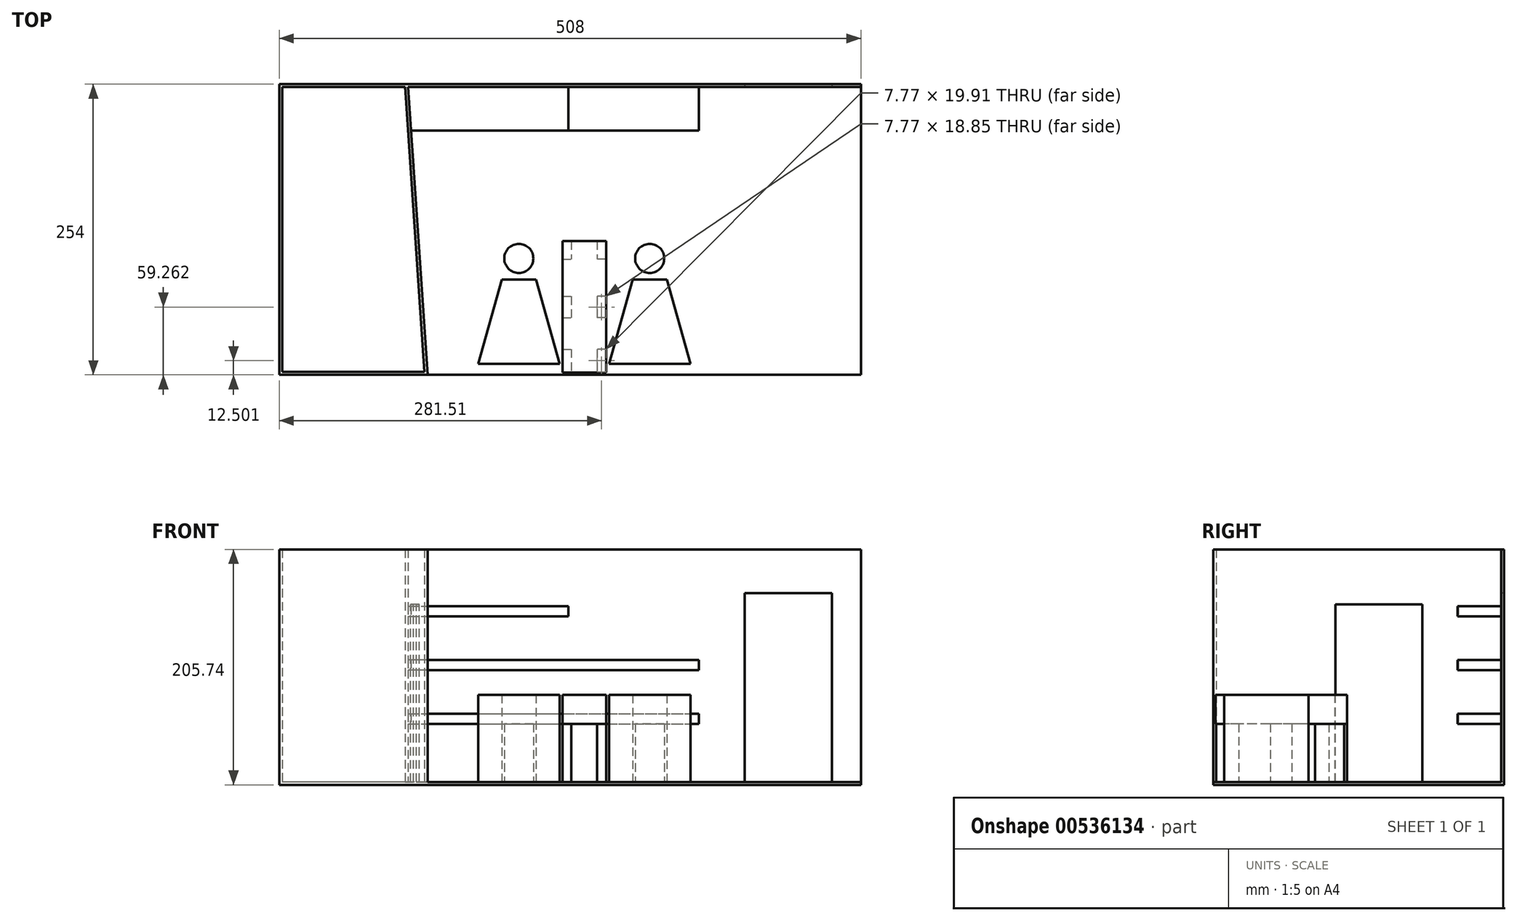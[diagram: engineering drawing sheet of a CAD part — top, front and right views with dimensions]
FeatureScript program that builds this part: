
annotation { "Feature Type Name" : "Feature", "Feature Type Description" : "" }
export const myFeature = defineFeature(function(context is Context, id is Id, definition is map)
    precondition{}
    {
        {
            var Q0;
            Q0=qCreatedBy(makeId("Top.planeOp"),FACE);
            var sketch = newSketch(context, id + "F0", { "sketchPlane" : qUnion([Q0])});
            skLineSegment(sketch, "E0.bottom", {"start": v(-252.39, 62) * mm, "end": v(255.61, 62) * mm});
            skLineSegment(sketch, "E0.top", {"start": v(-252.39, -192) * mm, "end": v(255.61, -192) * mm});
            skLineSegment(sketch, "E0.left", {"start": v(-252.39, 62) * mm, "end": v(-252.39, -192) * mm});
            skLineSegment(sketch, "E0.right", {"start": v(255.61, 62) * mm, "end": v(255.61, -192) * mm});
            skSolve(sketch);
        }
        {
            var Q0;
            Q0=makeQuery(id+"F0.imprint","IMPRINT",FACE,{"disambiguationData":[TD([[makeQuery(id+"F0.imprint","IMPRINT",EDGE,{"derivedFrom":sQuery(id+"F0.wireOp",EDGE,"E0.bottom")}),-1.0]])]});
            extrude(context, id + "F1", {"entities" : qUnion([Q0]), "depth" : 2.54 * mm, "offsetDistance" : 25.4 * mm});
        }
        {
            var Q0;
            Q0=makeQuery(id+"F1.opExtrude","CAP_FACE",FACE,{"disambiguationData":[OSD([sQuery(id+"F0.wireOp",EDGE,"E0.bottom"),sQuery(id+"F0.wireOp",EDGE,"E0.top"),sQuery(id+"F0.wireOp",EDGE,"E0.left"),sQuery(id+"F0.wireOp",EDGE,"E0.right")])],"isStart":false});
            var sketch = newSketch(context, id + "F2", { "sketchPlane" : qUnion([Q0])});
            skLineSegment(sketch, "E1", {"start": v(-252.39, -192) * mm, "end": v(-252.39, 62) * mm});
            skLineSegment(sketch, "E2", {"start": v(-252.39, 62) * mm, "end": v(255.61, 62) * mm});
            skLineSegment(sketch, "E3", {"start": v(255.61, 62) * mm, "end": v(255.61, 59.45) * mm});
            skLineSegment(sketch, "E4", {"start": v(255.61, 59.45) * mm, "end": v(-249.85, 59.45) * mm});
            skLineSegment(sketch, "E5", {"start": v(-249.85, 59.45) * mm, "end": v(-249.85, -192) * mm});
            skLineSegment(sketch, "E6", {"start": v(-249.85, -192) * mm, "end": v(-252.39, -192) * mm});
            skSolve(sketch);
        }
        {
            var Q0;
            Q0 = qSketchRegion(id + "F2", true);
            extrude(context, id + "F3", {"entities" : qUnion([Q0]), "operationType" : NewBodyOperationType.ADD, "depth" : 203.2 * mm, "offsetDistance" : 25.4 * mm});
        }
        {
            var Q0;
            Q0=makeQuery(id+"F1.opExtrude","CAP_FACE",FACE,{"disambiguationData":[OSD([sQuery(id+"F0.wireOp",EDGE,"E0.bottom"),sQuery(id+"F0.wireOp",EDGE,"E0.top"),sQuery(id+"F0.wireOp",EDGE,"E0.left"),sQuery(id+"F0.wireOp",EDGE,"E0.right")])],"isStart":false});
            var sketch = newSketch(context, id + "F4", { "sketchPlane" : qUnion([Q0])});
            skLineSegment(sketch, "E7.top", {"start": v(-249.85, -192) * mm, "end": v(-122.85, -192) * mm});
            skLineSegment(sketch, "E7.right", {"start": v(-139.97, 59.45) * mm, "end": v(-122.85, -192) * mm});
            skLineSegment(sketch, "E8", {"start": v(-139.97, 59.45) * mm, "end": v(-142.51, 59.45) * mm});
            skLineSegment(sketch, "E9", {"start": v(-142.51, 59.45) * mm, "end": v(-125.56, -189.47) * mm});
            skLineSegment(sketch, "E10", {"start": v(-125.56, -189.47) * mm, "end": v(-249.85, -189.47) * mm});
            skLineSegment(sketch, "E11", {"start": v(-249.85, -189.47) * mm, "end": v(-249.85, -192) * mm});
            skSolve(sketch);
        }
        {
            var Q0;
            Q0 = qSketchRegion(id + "F4", true);
            extrude(context, id + "F5", {"entities" : qUnion([Q0]), "operationType" : NewBodyOperationType.ADD, "depth" : 203.2 * mm, "offsetDistance" : 25.4 * mm});
        }
        {
            var Q0;
            Q0=makeQuery(id+"F5.opExtrude","SWEPT_FACE",FACE,{"disambiguationData":[OSD([sQuery(id+"F4.wireOp",EDGE,"E7.right")])]});
            var sketch = newSketch(context, id + "F6", { "sketchPlane" : qUnion([Q0])});
            skLineSegment(sketch, "E12.bottom", {"start": v(-76.2, 2.54) * mm, "end": v(0, 2.54) * mm});
            skLineSegment(sketch, "E12.top", {"start": v(-76.2, 157.64) * mm, "end": v(0, 157.64) * mm});
            skLineSegment(sketch, "E12.left", {"start": v(-76.2, 2.54) * mm, "end": v(-76.2, 157.64) * mm});
            skLineSegment(sketch, "E12.right", {"start": v(0, 2.54) * mm, "end": v(0, 157.64) * mm});
            skSolve(sketch);
        }
        {
            var Q0;
            Q0 = qSketchRegion(id + "F6", true);
            extrude(context, id + "F7", {"entities" : qUnion([Q0]), "operationType" : NewBodyOperationType.REMOVE, "oppositeDirection" : true, "depth" : 25.4 * mm, "offsetDistance" : 25.4 * mm});
        }
        {
            var Q0;
            {var subQ1=sQuery(id+"F0.wireOp",EDGE,"E0.right");var subQ2=sQuery(id+"F0.wireOp",EDGE,"E0.top");var subQ3=makeQuery(id+"F1.opExtrude","CAP_FACE",FACE,{"disambiguationData":[OSD([sQuery(id+"F0.wireOp",EDGE,"E0.bottom"),subQ2,sQuery(id+"F0.wireOp",EDGE,"E0.left"),subQ1])],"isStart":false});Q0=makeQuery(id+"F7.boolean.opBoolean","MERGE",FACE,{"derivedFrom":[makeQuery(id+"F5.boolean.opBoolean","SPLIT",FACE,{"disambiguationData":[TD([makeQuery(id+"F1.opExtrude","SWEPT_FACE",FACE,{"disambiguationData":[OSD([subQ2])]})])],"derivedFrom":subQ3}),makeQuery(id+"F5.boolean.opBoolean","SPLIT",FACE,{"disambiguationData":[TD([makeQuery(id+"F3.opExtrude","SWEPT_FACE",FACE,{"disambiguationData":[OSD([sQuery(id+"F2.wireOp",EDGE,"E5")])]})])],"derivedFrom":subQ3}),makeQuery(id+"F7.opExtrude","SWEPT_FACE",FACE,{"disambiguationData":[OSD([sQuery(id+"F6.wireOp",EDGE,"E12.bottom")])]})]});}
            var sketch = newSketch(context, id + "F8", { "sketchPlane" : qUnion([Q0])});
            skLineSegment(sketch, "E13", {"start": v(-43.2, -182.35) * mm, "end": v(-7.63, -182.35) * mm});
            skLineSegment(sketch, "E14", {"start": v(-7.63, -182.35) * mm, "end": v(-28.26, -108.75) * mm});
            skLineSegment(sketch, "E15", {"start": v(-28.26, -108.75) * mm, "end": v(-43.2, -108.75) * mm});
            skPoint(sketch, "E15.endSnap0", {"position": v(-43.2, -182.35) * mm});
            skLineSegment(sketch, "E16", {"start": v(-43.2, -108.75) * mm, "end": v(-43.2, -182.35) * mm, "construction": true});
            skPoint(sketch, "E17.orphan", {"position": v(-78.75, -182.35) * mm});
            skLineSegment(sketch, "E18.MirrorCS", {"start": v(-78.75, -182.35) * mm, "end": v(-58.13, -108.75) * mm});
            skLineSegment(sketch, "E19.MirrorCS", {"start": v(-58.13, -108.75) * mm, "end": v(-43.2, -108.75) * mm});
            skLineSegment(sketch, "E20.MirrorCS", {"start": v(-43.2, -182.35) * mm, "end": v(-78.75, -182.35) * mm});
            skSolve(sketch);
        }
        {
            var Q0;
            Q0=makeQuery(id+"F8.imprint","IMPRINT",FACE,{"disambiguationData":[TD([[makeQuery(id+"F8.imprint","IMPRINT",EDGE,{"derivedFrom":sQuery(id+"F8.wireOp",EDGE,"E13")}),1.0]])]});
            extrude(context, id + "F9", {"entities" : qUnion([Q0]), "operationType" : NewBodyOperationType.ADD, "depth" : 76.2 * mm, "offsetDistance" : 25.4 * mm});
        }
        {
            var Q0;
            {var subQ1=sQuery(id+"F0.wireOp",EDGE,"E0.right");var subQ2=sQuery(id+"F0.wireOp",EDGE,"E0.top");var subQ3=makeQuery(id+"F1.opExtrude","CAP_FACE",FACE,{"disambiguationData":[OSD([sQuery(id+"F0.wireOp",EDGE,"E0.bottom"),subQ2,sQuery(id+"F0.wireOp",EDGE,"E0.left"),subQ1])],"isStart":false});Q0=makeQuery(id+"F7.boolean.opBoolean","MERGE",FACE,{"derivedFrom":[makeQuery(id+"F5.boolean.opBoolean","SPLIT",FACE,{"disambiguationData":[TD([makeQuery(id+"F1.opExtrude","SWEPT_FACE",FACE,{"disambiguationData":[OSD([subQ2])]})])],"derivedFrom":subQ3}),makeQuery(id+"F5.boolean.opBoolean","SPLIT",FACE,{"disambiguationData":[TD([makeQuery(id+"F3.opExtrude","SWEPT_FACE",FACE,{"disambiguationData":[OSD([sQuery(id+"F2.wireOp",EDGE,"E5")])]})])],"derivedFrom":subQ3}),makeQuery(id+"F7.opExtrude","SWEPT_FACE",FACE,{"disambiguationData":[OSD([sQuery(id+"F6.wireOp",EDGE,"E12.bottom")])]})]});}
            var sketch = newSketch(context, id + "F10", { "sketchPlane" : qUnion([Q0])});
            skLineSegment(sketch, "E21.bottom", {"start": v(-5.1, -189.47) * mm, "end": v(33, -189.47) * mm, "construction": true});
            skLineSegment(sketch, "E21.top", {"start": v(-5.1, -75.17) * mm, "end": v(33, -75.17) * mm, "construction": true});
            skLineSegment(sketch, "E21.left", {"start": v(-5.1, -189.47) * mm, "end": v(-5.1, -75.17) * mm, "construction": true});
            skLineSegment(sketch, "E21.right", {"start": v(33, -189.47) * mm, "end": v(33, -75.17) * mm, "construction": true});
            skLineSegment(sketch, "E22.bottom", {"start": v(-5.1, -75.17) * mm, "end": v(2.68, -75.17) * mm});
            skLineSegment(sketch, "E22.top", {"start": v(-5.1, -90.97) * mm, "end": v(2.68, -90.97) * mm});
            skLineSegment(sketch, "E22.left", {"start": v(-5.1, -75.17) * mm, "end": v(-5.1, -90.97) * mm});
            skLineSegment(sketch, "E22.right", {"start": v(2.68, -75.17) * mm, "end": v(2.68, -90.97) * mm});
            skLineSegment(sketch, "E23.bottom", {"start": v(-5.1, -123.32) * mm, "end": v(2.68, -123.32) * mm});
            skLineSegment(sketch, "E23.top", {"start": v(-5.1, -142.17) * mm, "end": v(2.68, -142.17) * mm});
            skLineSegment(sketch, "E23.left", {"start": v(-5.1, -123.32) * mm, "end": v(-5.1, -142.17) * mm});
            skLineSegment(sketch, "E23.right", {"start": v(2.68, -123.32) * mm, "end": v(2.68, -142.17) * mm});
            skLineSegment(sketch, "E24.bottom", {"start": v(-5.1, -169.55) * mm, "end": v(2.68, -169.55) * mm});
            skLineSegment(sketch, "E24.top", {"start": v(-5.1, -189.47) * mm, "end": v(2.68, -189.47) * mm});
            skLineSegment(sketch, "E24.left", {"start": v(-5.1, -169.55) * mm, "end": v(-5.1, -189.47) * mm});
            skLineSegment(sketch, "E24.right", {"start": v(2.68, -169.55) * mm, "end": v(2.68, -189.47) * mm});
            skLineSegment(sketch, "E25", {"start": v(13.96, -75.17) * mm, "end": v(13.96, -189.47) * mm, "construction": true});
            skLineSegment(sketch, "E26.MirrorCS", {"start": v(25.23, -75.17) * mm, "end": v(25.23, -90.97) * mm});
            skLineSegment(sketch, "E27.MirrorCS", {"start": v(33, -90.97) * mm, "end": v(25.23, -90.97) * mm});
            skLineSegment(sketch, "E28.MirrorCS", {"start": v(33, -123.32) * mm, "end": v(25.23, -123.32) * mm});
            skLineSegment(sketch, "E29.MirrorCS", {"start": v(25.23, -123.32) * mm, "end": v(25.23, -142.17) * mm});
            skLineSegment(sketch, "E30.MirrorCS", {"start": v(33, -142.17) * mm, "end": v(25.23, -142.17) * mm});
            skLineSegment(sketch, "E31.MirrorCS", {"start": v(33, -169.55) * mm, "end": v(25.23, -169.55) * mm});
            skLineSegment(sketch, "E32.MirrorCS", {"start": v(25.23, -169.55) * mm, "end": v(25.23, -189.47) * mm});
            skLineSegment(sketch, "E33", {"start": v(25.23, -75.17) * mm, "end": v(33, -75.17) * mm, "construction": true});
            skLineSegment(sketch, "E34", {"start": v(33, -75.17) * mm, "end": v(25.23, -75.17) * mm});
            skLineSegment(sketch, "E35", {"start": v(33, -75.17) * mm, "end": v(33, -90.97) * mm});
            skLineSegment(sketch, "E36", {"start": v(33, -123.32) * mm, "end": v(33, -142.17) * mm});
            skLineSegment(sketch, "E37", {"start": v(33, -169.55) * mm, "end": v(33, -189.47) * mm});
            skLineSegment(sketch, "E38.MirrorCS", {"start": v(56.17, -108.75) * mm, "end": v(86.04, -108.75) * mm});
            skLineSegment(sketch, "E39.MirrorCS", {"start": v(35.55, -182.35) * mm, "end": v(56.17, -108.75) * mm});
            skLineSegment(sketch, "E40.MirrorCS", {"start": v(86.04, -108.75) * mm, "end": v(106.67, -182.35) * mm});
            skLineSegment(sketch, "E41.MirrorCS", {"start": v(106.67, -182.35) * mm, "end": v(35.55, -182.35) * mm});
            skLineSegment(sketch, "E42", {"start": v(25.23, -189.47) * mm, "end": v(33, -189.47) * mm});
            skPoint(sketch, "E43.0.0.start.orphan", {"position": v(-58.13, -108.75) * mm});
            skPoint(sketch, "E43.0.2.end.orphan", {"position": v(-28.26, -108.75) * mm});
            skPoint(sketch, "E43.0.1.end.orphan", {"position": v(-7.63, -182.35) * mm});
            skPoint(sketch, "E43.0.1.start.orphan", {"position": v(-78.75, -182.35) * mm});
            skSolve(sketch);
        }
        {
            var Q0;
            Q0 = qSketchRegion(id + "F10", true);
            extrude(context, id + "F11", {"entities" : qUnion([Q0]), "operationType" : NewBodyOperationType.ADD, "depth" : 76.2 * mm, "offsetDistance" : 25.4 * mm});
        }
        {
            var Q0;
            Q0=makeQuery(id+"F11.opExtrude","CAP_FACE",FACE,{"disambiguationData":[OSD([sQuery(id+"F10.wireOp",EDGE,"E22.bottom"),sQuery(id+"F10.wireOp",EDGE,"E22.top"),sQuery(id+"F10.wireOp",EDGE,"E22.left"),sQuery(id+"F10.wireOp",EDGE,"E22.right")])],"isStart":false});
            var sketch = newSketch(context, id + "F12", { "sketchPlane" : qUnion([Q0])});
            skLineSegment(sketch, "E44.bottom", {"start": v(-5.1, -75.17) * mm, "end": v(33.24, -75.17) * mm});
            skLineSegment(sketch, "E44.top", {"start": v(-5.1, -189.9) * mm, "end": v(33.24, -189.9) * mm});
            skLineSegment(sketch, "E44.left", {"start": v(-5.1, -75.17) * mm, "end": v(-5.1, -189.9) * mm});
            skLineSegment(sketch, "E44.right", {"start": v(33.24, -75.17) * mm, "end": v(33.24, -189.9) * mm});
            skSolve(sketch);
        }
        {
            var Q0;
            Q0 = qSketchRegion(id + "F12", true);
            extrude(context, id + "F13", {"entities" : qUnion([Q0]), "operationType" : NewBodyOperationType.ADD, "oppositeDirection" : true, "depth" : 25.4 * mm, "offsetDistance" : 25.4 * mm});
        }
        {
            var Q0;
            {var subQ1=sQuery(id+"F0.wireOp",EDGE,"E0.right");var subQ2=sQuery(id+"F0.wireOp",EDGE,"E0.top");var subQ3=makeQuery(id+"F1.opExtrude","CAP_FACE",FACE,{"disambiguationData":[OSD([sQuery(id+"F0.wireOp",EDGE,"E0.bottom"),subQ2,sQuery(id+"F0.wireOp",EDGE,"E0.left"),subQ1])],"isStart":false});Q0=makeQuery(id+"F7.boolean.opBoolean","MERGE",FACE,{"derivedFrom":[makeQuery(id+"F5.boolean.opBoolean","SPLIT",FACE,{"disambiguationData":[TD([makeQuery(id+"F1.opExtrude","SWEPT_FACE",FACE,{"disambiguationData":[OSD([subQ2])]})])],"derivedFrom":subQ3}),makeQuery(id+"F5.boolean.opBoolean","SPLIT",FACE,{"disambiguationData":[TD([makeQuery(id+"F3.opExtrude","SWEPT_FACE",FACE,{"disambiguationData":[OSD([sQuery(id+"F2.wireOp",EDGE,"E5")])]})])],"derivedFrom":subQ3}),makeQuery(id+"F7.opExtrude","SWEPT_FACE",FACE,{"disambiguationData":[OSD([sQuery(id+"F6.wireOp",EDGE,"E12.bottom")])]})]});}
            var sketch = newSketch(context, id + "F14", { "sketchPlane" : qUnion([Q0])});
            skCircle(sketch, "E45", {"center": v(-43.2, -90.25) * mm, "radius": 12.7 * mm});
            skPoint(sketch, "E45.centerSnap0", {"position": v(-43.2, -108.75) * mm});
            skCircle(sketch, "E46", {"center": v(71.1, -90.25) * mm, "radius": 12.7 * mm});
            skPoint(sketch, "E47", {"position": v(71.1, -108.75) * mm});
            skSolve(sketch);
        }
        {
            var Q0;
            Q0 = qSketchRegion(id + "F14", true);
            extrude(context, id + "F15", {"entities" : qUnion([Q0]), "operationType" : NewBodyOperationType.ADD, "depth" : 50.8 * mm, "offsetDistance" : 25.4 * mm});
        }
        {
            var Q0;
            {var subQ0=sQuery(id+"F2.wireOp",EDGE,"E4");var subQ2=sQuery(id+"F0.wireOp",EDGE,"E0.right");Q0=makeQuery(id+"F5.boolean.opBoolean","SPLIT",FACE,{"disambiguationData":[TD([makeQuery(id+"F1.opExtrude","SWEPT_FACE",FACE,{"disambiguationData":[OSD([subQ2])]})])],"derivedFrom":makeQuery(id+"F3.opExtrude","SWEPT_FACE",FACE,{"disambiguationData":[OSD([subQ0])]})});}
            var sketch = newSketch(context, id + "F16", { "sketchPlane" : qUnion([Q0])});
            skLineSegment(sketch, "E48.bottom", {"start": v(154.01, 2.54) * mm, "end": v(230.21, 2.54) * mm});
            skLineSegment(sketch, "E48.top", {"start": v(154.01, 167.64) * mm, "end": v(230.21, 167.64) * mm});
            skLineSegment(sketch, "E48.left", {"start": v(154.01, 2.54) * mm, "end": v(154.01, 167.64) * mm});
            skLineSegment(sketch, "E48.right", {"start": v(230.21, 2.54) * mm, "end": v(230.21, 167.64) * mm});
            skSolve(sketch);
        }
        {
            var Q0;
            Q0 = qSketchRegion(id + "F16", true);
            extrude(context, id + "F17", {"entities" : qUnion([Q0]), "operationType" : NewBodyOperationType.REMOVE, "oppositeDirection" : true, "depth" : 25.4 * mm, "offsetDistance" : 25.4 * mm});
        }
        {
            var Q0;
            {var subQ0=sQuery(id+"F2.wireOp",EDGE,"E4");var subQ2=sQuery(id+"F0.wireOp",EDGE,"E0.right");Q0=makeQuery(id+"F5.boolean.opBoolean","SPLIT",FACE,{"disambiguationData":[TD([makeQuery(id+"F1.opExtrude","SWEPT_FACE",FACE,{"disambiguationData":[OSD([subQ2])]})])],"derivedFrom":makeQuery(id+"F3.opExtrude","SWEPT_FACE",FACE,{"disambiguationData":[OSD([subQ0])]})});}
            var sketch = newSketch(context, id + "F18", { "sketchPlane" : qUnion([Q0])});
            skLineSegment(sketch, "E49.bottom", {"start": v(-139.97, 53.34) * mm, "end": v(114.03, 53.34) * mm});
            skLineSegment(sketch, "E49.top", {"start": v(-139.97, 62.23) * mm, "end": v(114.03, 62.23) * mm});
            skLineSegment(sketch, "E49.left", {"start": v(-139.97, 53.34) * mm, "end": v(-139.97, 62.23) * mm});
            skLineSegment(sketch, "E49.right", {"start": v(114.03, 53.34) * mm, "end": v(114.03, 62.23) * mm});
            skLineSegment(sketch, "E50.bottom", {"start": v(114.03, 109.22) * mm, "end": v(-139.97, 109.22) * mm});
            skLineSegment(sketch, "E50.top", {"start": v(114.03, 100.33) * mm, "end": v(-139.97, 100.33) * mm});
            skLineSegment(sketch, "E50.left", {"start": v(114.03, 109.22) * mm, "end": v(114.03, 100.33) * mm});
            skLineSegment(sketch, "E50.right", {"start": v(-139.97, 109.22) * mm, "end": v(-139.97, 100.33) * mm});
            skLineSegment(sketch, "E51.bottom", {"start": v(-139.97, 147.32) * mm, "end": v(0, 147.32) * mm});
            skLineSegment(sketch, "E51.top", {"start": v(-139.97, 156.21) * mm, "end": v(0, 156.21) * mm});
            skLineSegment(sketch, "E51.left", {"start": v(-139.97, 147.32) * mm, "end": v(-139.97, 156.21) * mm});
            skLineSegment(sketch, "E51.right", {"start": v(0, 147.32) * mm, "end": v(0, 156.21) * mm});
            skSolve(sketch);
        }
        {
            var Q0;
            Q0 = qSketchRegion(id + "F18", true);
            extrude(context, id + "F19", {"entities" : qUnion([Q0]), "operationType" : NewBodyOperationType.ADD, "depth" : 38.1 * mm, "offsetDistance" : 25.4 * mm});
        }
    });
